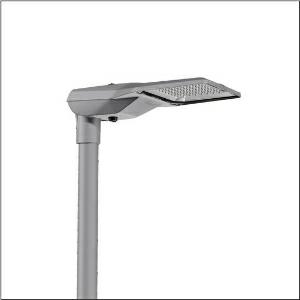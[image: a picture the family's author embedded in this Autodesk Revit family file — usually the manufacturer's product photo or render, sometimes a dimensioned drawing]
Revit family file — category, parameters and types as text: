
# Revit family: streetlight_sl_21_midi___st1_0ab_5xe3m32y08nb_2421
name_source: partatom
category: Lighting Fixtures
units: mm (PartAtom-declared; Revit-internal decimal feet)

## family parameters
Cut with Voids When Loaded = No
Host = Face
Light Source = No
Part Type = Normal
Room Calculation Point = No
Round Connector Dimension = Use Diameter
Shared = No

## types (1)
- --- (1 x LED, 19980 lm, 151.2 W, 3000K)
    Apparent Load = 151 VA
    CIE Flux Codes = 40 74 97 100 100
    Color Rendering = 70
    Color Temperature = 3000K
    Default Elevation = 1800 mm
    Description = Streetlight SL 21 midi, mast luminaire, primary light control with lens, of PMMA, primary optical cover: cover, of toughened safety glass, transparent, light distribution: ST1.0aB, light emission: direct distribution, primary light characteristic: asymmetric, installation type: side-entry, post-top, LED, High Power LED, rated luminous flux: 19.980lm, luminous efficacy: 132lm/W, light colour: 730, colour temperature: 3000K, control gear: D4i with power reduction, control: flexible luminous flux parameterisation, time-dependent luminous flux control, constant luminous flux control, overheat protection, power reduction, pre-setting: logarithmic dimming characteristic, mains connection: 230..240V, AC, 50/60Hz, start of lifetime: 151W, end of service life: 157W, reduction: 70W, luminaire housing, of diecast aluminium, powder-coated, Siteco® metallic grey (DB 702S), corrosivity category C5 mid according to DIN EN ISO 12944, please order mast flange separately, inclination adjustable: 0°, 5°, 10°, 15°, sealing non-destructively replaceable, multi-level sealing system, length: 644mm, width: 335mm, height: 110mm, mast flange for spigot size: 42mm (side-entry): 5XC10008XM4, 60/48mm (side-entry/post-top): 5XC10108XM2, 76/60mm (side-entry/post-top): 5XC10108XM1, mounting height: 4..8m, Smart Interface below and above, protection rating (complete): IP66, insulation class (complete): insulation class II (safety insulation), certification: CE, ENEC, ENEC+, VDE, impact resistance: IK10, permissible operating ambient temperature for outdoor applications: -40..+50°C, standard-compliant lighting for roads and squares, packaging unit: 1 piece

Light Distribution: ST1.0aB
    Height = 111 mm
    Lamp = 1 x LED
    Lamp Light Flux = 19980 lm
    Lamp Power = 151.2 W
    Lamp count = 1
    Length = 644 mm
    Luminous efficacy = 132 lm/W
    Manufacturer = Siteco
    ModVariant = No
    Model = 5XE3M32Y08NB
    Number of Poles = 1
    OnlyDefault = Yes
    Power Factor = 1
    Product Name = Streetlight SL 21 midi | ST1.0aB
    Product group = mast luminaire | pylon top
    ProductGroupID = 6100
    Protection Class = Protection class II
    Protection Degree = IP 66
    RLX_Detail_Level = 1
    RLX_Emergency_Light_Flux = 0 lm
    RLX_Emergency_Type = 0
    RLX_Emergency_Type_DB = No
    RlxData = <blob elided: 27089 chars, md5=78796a32>
    Socket = socket
    Standby Power = 0 W
    System Light Flux = 19980 lm
    System Power = 151 W
    Type Comments = factory setting: luminous flux: 100 % | dim-lin: 254 | 802 mA
    Type Image = l_1004304.jpg
    URL = http://relux.com
    VarID = @adj_168070
    Voltage = 0 V
    Weight = 0.00 kg
    Width = 336 mm

## geometry (parser evidence)
native form markers: Blend x4, Sweep x10
no freeform markers — native parametric forms only
